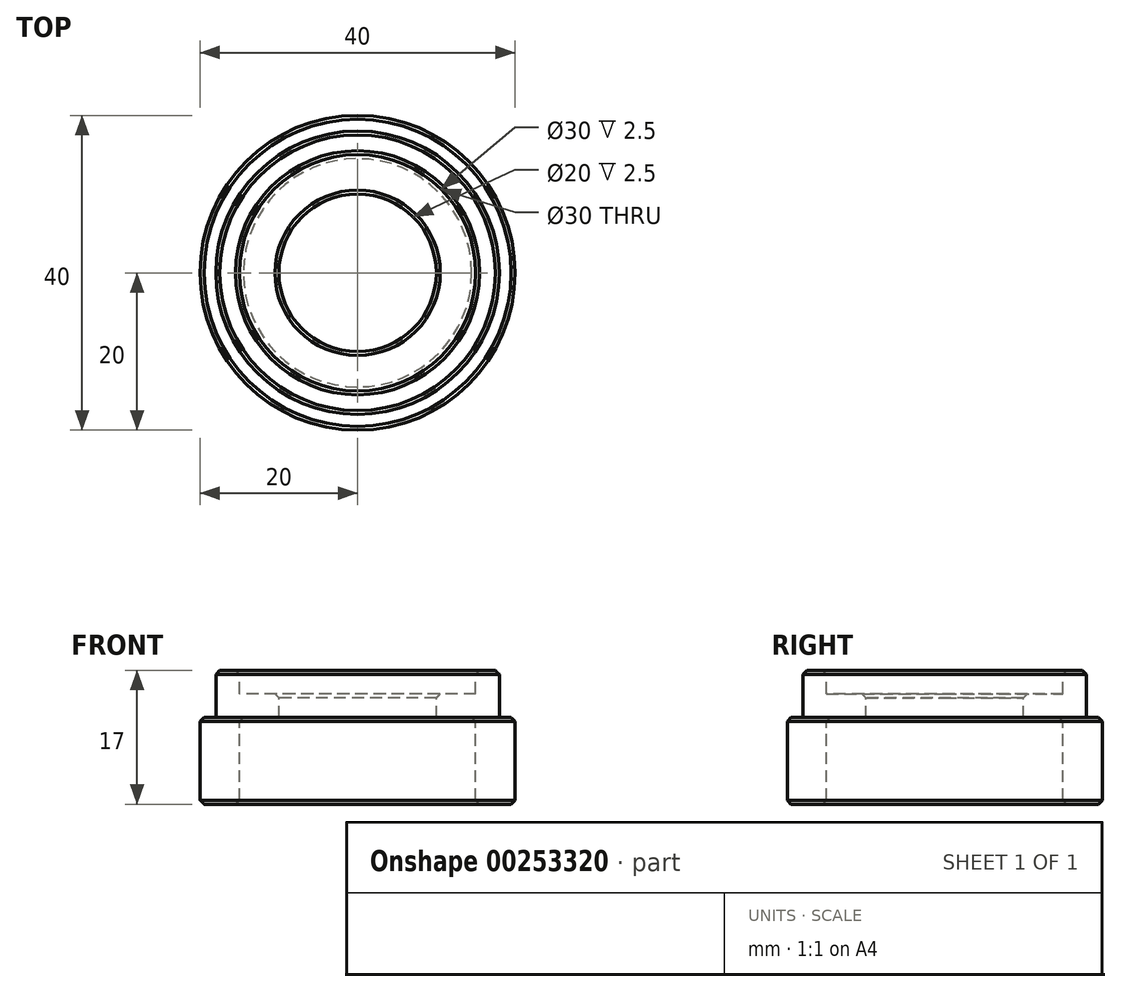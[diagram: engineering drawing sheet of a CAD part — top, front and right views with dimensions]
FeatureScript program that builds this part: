
annotation { "Feature Type Name" : "Feature", "Feature Type Description" : "" }
export const myFeature = defineFeature(function(context is Context, id is Id, definition is map)
    precondition{}
    {
        {
            var Q0;
            Q0=qCreatedBy(makeId("Front.planeOp"),FACE);
            var sketch = newSketch(context, id + "F0", { "sketchPlane" : qUnion([Q0])});
            skLineSegment(sketch, "E0", {"start": v(15, 17) * mm, "end": v(18, 17) * mm});
            skLineSegment(sketch, "E1", {"start": v(18, 17) * mm, "end": v(18, 11) * mm});
            skLineSegment(sketch, "E2", {"start": v(18, 11) * mm, "end": v(20, 11) * mm});
            skLineSegment(sketch, "E3", {"start": v(20, 11) * mm, "end": v(20, 0) * mm});
            skLineSegment(sketch, "E4", {"start": v(20, 0) * mm, "end": v(15, 0) * mm});
            skLineSegment(sketch, "E5", {"start": v(15, 0) * mm, "end": v(15, 11) * mm});
            skLineSegment(sketch, "E6", {"start": v(15, 11) * mm, "end": v(10, 11) * mm});
            skLineSegment(sketch, "E7", {"start": v(10, 11) * mm, "end": v(10, 14) * mm});
            skLineSegment(sketch, "E8", {"start": v(10, 14) * mm, "end": v(15, 14) * mm});
            skLineSegment(sketch, "E9", {"start": v(15, 14) * mm, "end": v(15, 17) * mm});
            skLineSegment(sketch, "E10", {"start": v(0, 29.26) * mm, "end": v(0, -12.7) * mm});
            skSolve(sketch);
        }
        {
            var Q0;
            Q0=makeQuery(id+"F0.imprint","IMPRINT",FACE,{"disambiguationData":[TD([[makeQuery(id+"F0.imprint","IMPRINT",EDGE,{"derivedFrom":sQuery(id+"F0.wireOp",EDGE,"E0")}),-1.0]])]});
            var Q1;
            Q1=sQuery(id+"F0.wireOp",EDGE,"E10");
            revolve(context, id + "F1", {"entities" : qUnion([Q0]), "axis" : qUnion([Q1]), "revolveType" : RevolveType.FULL});
        }
        {
            var Q0;
            Q0=makeQuery(id+"F1.opRevolve","SWEPT_EDGE",EDGE,{"disambiguationData":[OSD([sQuery(id+"F0.wireOp",EDGE,"E0"),sQuery(id+"F0.wireOp",EDGE,"E9")])]});
            var Q1;
            Q1=makeQuery(id+"F1.opRevolve","SWEPT_EDGE",EDGE,{"disambiguationData":[OSD([sQuery(id+"F0.wireOp",EDGE,"E7"),sQuery(id+"F0.wireOp",EDGE,"E8")])]});
            var Q2;
            Q2=makeQuery(id+"F1.opRevolve","SWEPT_EDGE",EDGE,{"disambiguationData":[OSD([sQuery(id+"F0.wireOp",EDGE,"E5"),sQuery(id+"F0.wireOp",EDGE,"E6")])]});
            var Q3;
            Q3=makeQuery(id+"F1.opRevolve","SWEPT_EDGE",EDGE,{"disambiguationData":[OSD([sQuery(id+"F0.wireOp",EDGE,"E4"),sQuery(id+"F0.wireOp",EDGE,"E5")])]});
            var Q4;
            Q4=makeQuery(id+"F1.opRevolve","SWEPT_EDGE",EDGE,{"disambiguationData":[OSD([sQuery(id+"F0.wireOp",EDGE,"E2"),sQuery(id+"F0.wireOp",EDGE,"E3")])]});
            var Q5;
            Q5=makeQuery(id+"F1.opRevolve","SWEPT_EDGE",EDGE,{"disambiguationData":[OSD([sQuery(id+"F0.wireOp",EDGE,"E0"),sQuery(id+"F0.wireOp",EDGE,"E1")])]});
            var Q6;
            Q6=makeQuery(id+"F1.opRevolve","SWEPT_EDGE",EDGE,{"disambiguationData":[OSD([sQuery(id+"F0.wireOp",EDGE,"E3"),sQuery(id+"F0.wireOp",EDGE,"E4")])]});
            chamfer(context, id + "F2", {"entities" : qUnion([Q0, Q1, Q2, Q3, Q4, Q5, Q6]), "chamferType" : ChamferType.OFFSET_ANGLE, "width" : .5 * mm, "oppositeDirection" : false, "angle" : 45 * degree, "tangentPropagation" : true});
        }
    });
